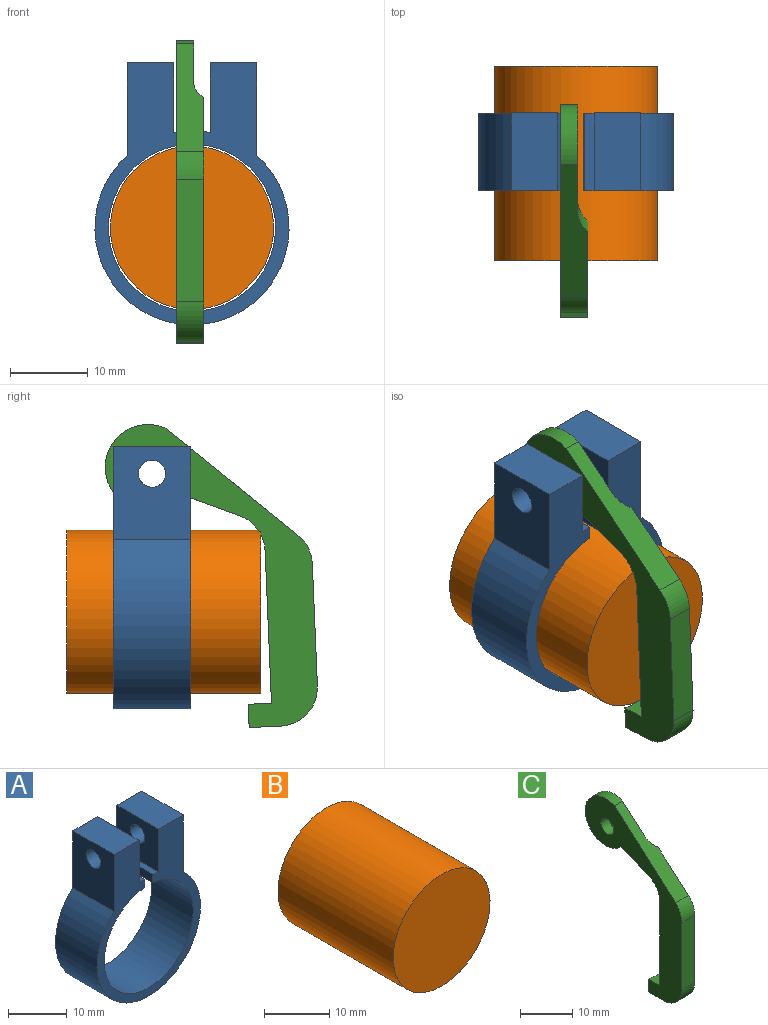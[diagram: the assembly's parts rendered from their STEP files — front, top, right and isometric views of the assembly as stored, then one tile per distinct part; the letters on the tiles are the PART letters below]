
ASSEMBLY  parts=3 mates=2
PART A: 16 faces, bbox 25x10x33.7 mm
  f0: plane 10x1.76mm, normal (1,0,0.01), area 17.6mm2, adj f1,f11,f12,f13
  f1: cylinder r=12.5mm len=10mm, axis (0,1,0), area 13mm2, adj f0,f2,f12,f13
  f2: plane 10x8.95mm, normal (1,0,0), area 79.8mm2, adj f1,f3,f12,f13,f15
  f3: plane 10x6mm, normal (0,0,1), area 60mm2, adj f2,f4,f12,f13
  f4: plane 11.91x10mm, normal (-1,0,0), area 109.5mm2, adj f3,f5,f12,f13,f15
  f5: cylinder r=12.5mm len=25mm, axis (0,1,0), area 603mm2, adj f4,f6,f12,f13
  f6: plane 11.91x10mm, normal (1,0,0), area 109.5mm2, adj f5,f7,f12,f13,f14
  f7: plane 10x6mm, normal (0,0,1), area 60mm2, adj f6,f8,f12,f13
  f8: plane 10x8.95mm, normal (-1,0,0), area 79.8mm2, adj f7,f9,f12,f13,f14
  f9: cylinder r=12.5mm len=10mm, axis (0,1,0), area 13mm2, adj f8,f10,f12,f13
  f10: plane 10x1.76mm, normal (-1,0,0.01), area 17.6mm2, adj f9,f11,f12,f13
  f11: cylinder r=10.75mm len=21.5mm, axis (0,1,0), area 654.9mm2, adj f0,f10,f12,f13
  f12: plane 33.73x25mm, normal (0,-1,0), area 245.3mm2, adj f0,f1,f2,f3,f4,f5,f6,f7
  f13: plane 33.73x25mm, normal (0,1,0), area 245.3mm2, adj f0,f1,f2,f3,f4,f5,f6,f7
  f14: cylinder r=1.75mm len=6mm, axis (1,0,0), area 66mm2, adj f6,f8
  f15: cylinder r=1.75mm len=6mm, axis (1,0,0), area 66mm2, adj f2,f4
PART B: 3 faces, bbox 21x25x21 mm
  f0: cylinder r=10.5mm len=25mm, axis (0,1,0), area 1649.3mm2, adj f1,f2
  f1: plane 21x21mm, normal (0,-1,0), area 346.4mm2, adj f0
  f2: plane 21x21mm, normal (0,1,0), area 346.4mm2, adj f0
PART C: 16 faces, bbox 3.5x26.1x39.5 mm
  f0: plane 16.51x14.48mm, normal (0,-0.66,0.75), area 63.8mm2, adj f2,f5,f6,f12,f13,f14
  f1: plane 7.38x3.5mm, normal (0,0.38,-0.92), area 22mm2, adj f2,f5,f6,f13,f14,f15
  f2: cylinder r=5.52mm len=11.05mm, axis (-1,0,0), area 53.9mm2, adj f0,f1,f6,f13
  f3: cylinder r=1.75mm len=3.5mm, axis (1,0,0), area 24.2mm2, adj f6,f13
  f4: plane 19.83x3.5mm, normal (0,1,0), area 69.2mm2, adj f5,f6,f9,f15
  f5: plane 31.74x11.41mm, normal (1,0,0), area 174mm2, adj f0,f1,f4,f7,f8,f9,f10,f11
  f6: plane 39.52x26.13mm, normal (-1,0,0), area 286.6mm2, adj f0,f1,f2,f3,f4,f7,f8,f9
  f7: plane 15.73x3.5mm, normal (0,-1,0), area 55.1mm2, adj f5,f6,f11,f12
  f8: plane 4x3.5mm, normal (0,0,-1), area 14mm2, adj f5,f6,f10,f11
  f9: extruded ~3.5x3mm, area 10.5mm2, adj f4,f5,f6,f10
  f10: plane 3.5x2.99mm, normal (0,1,0), area 10.1mm2, adj f5,f6,f8,f9
  f11: cylinder r=5mm len=5mm, axis (1,0,0), area 27.5mm2, adj f5,f6,f7,f8
  f12: cylinder r=5mm len=3.76mm, axis (1,0,0), area 14.9mm2, adj f0,f5,f6,f7
  f13: plane 13.83x11.05mm, normal (1,0,0), area 99.7mm2, adj f0,f1,f2,f3,f14
  f14: cylinder r=4mm len=5.55mm, axis (0,-0.38,0.92), area 14.1mm2, adj f0,f1,f5,f13
  f15: cylinder r=5mm len=4.62mm, axis (1,0,0), area 20.6mm2, adj f1,f4,f5,f6
PLACE A at identity fixed
PLACE B t=(0,6,0)mm
PLACE C rot(axis=(-1,0,0),2.4deg) t=(-1.98,5.6,-0.35)mm
MATE revolute A.f14 <-> C.f3  axis (1,0,0) through (-2.33,-5,17.78)mm
MATE slider A.f5 <-> B.f0  axis (0,1,0) through (0,0,0)mm
